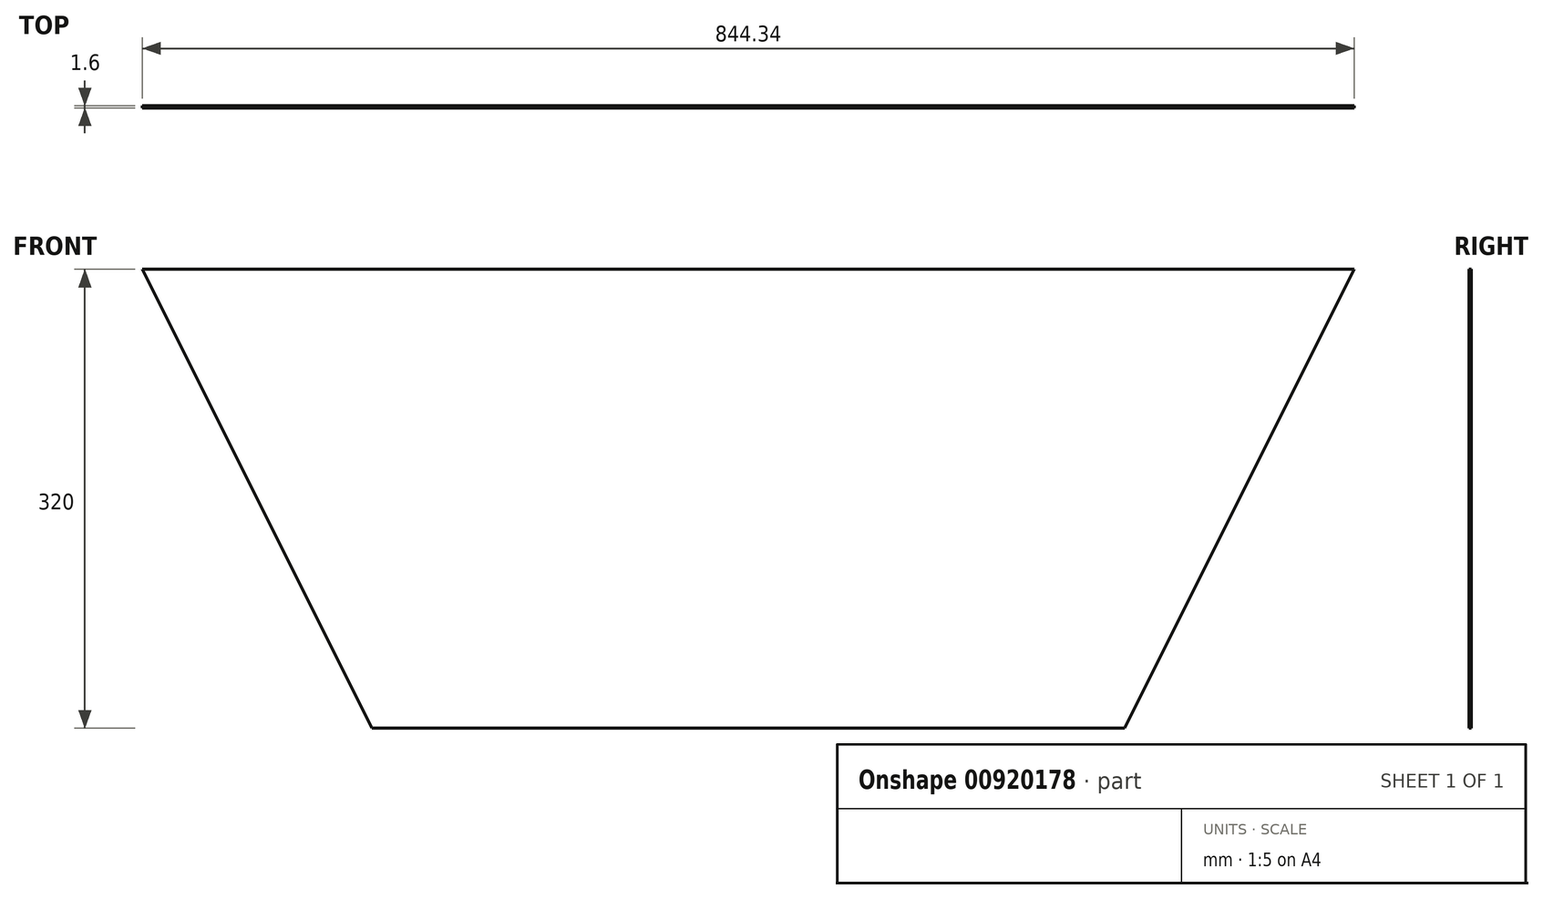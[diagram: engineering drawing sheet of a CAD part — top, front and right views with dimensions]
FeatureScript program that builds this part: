
annotation { "Feature Type Name" : "Feature", "Feature Type Description" : "" }
export const myFeature = defineFeature(function(context is Context, id is Id, definition is map)
    precondition{}
    {
        {
            var Q0;
            Q0=qCreatedBy(makeId("Front.planeOp"),FACE);
            var sketch = newSketch(context, id + "F0", { "sketchPlane" : qUnion([Q0])});
            skLineSegment(sketch, "E0", {"start": v(-422.17, 181.87) * mm, "end": v(-262.17, -138.13) * mm});
            skLineSegment(sketch, "E1", {"start": v(422.17, 181.87) * mm, "end": v(262.17, -138.13) * mm});
            skLineSegment(sketch, "E2", {"start": v(262.17, -138.13) * mm, "end": v(-262.17, -138.13) * mm});
            skLineSegment(sketch, "E3", {"start": v(422.17, 181.87) * mm, "end": v(-422.17, 181.87) * mm});
            skSolve(sketch);
        }
        {
            var Q0;
            Q0 = qSketchRegion(id + "F0", true);
            extrude(context, id + "F1", {"entities" : qUnion([Q0]), "depth" : 1.6 * mm, "offsetDistance" : 25 * mm});
        }
    });
